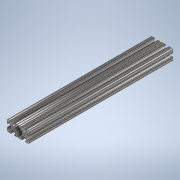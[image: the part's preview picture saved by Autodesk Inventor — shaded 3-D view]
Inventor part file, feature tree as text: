
AUTODESK INVENTOR PART (.ipt)
format: ipt  version: 2020 (Build 240168000, 168)  size: 344,064 bytes
history: native  units: in
note: dims shown in document units (in); Inventor stores cm internally (conversion verified against a paired STEP export)
features: sketch x2, extrude x1
ambient origin geometry x8: Origin, YZ Plane, XZ Plane, XY Plane, X Axis, Y Axis, Z Axis, Center Point
bodies: Solid1 (feature_tree)
feature tree (3):
  extrude  "Extrusion1"  [1 undecoded]
  sketch  "Sketch2"
  sketch  "Sketch1"  dims[d0=13.0in d1=0.0in]
note: 1 required parameter value undecoded (feature->parameter linkage not recoverable at this tier; creation-order binding heuristic only, values carry confidence <= 0.55)
